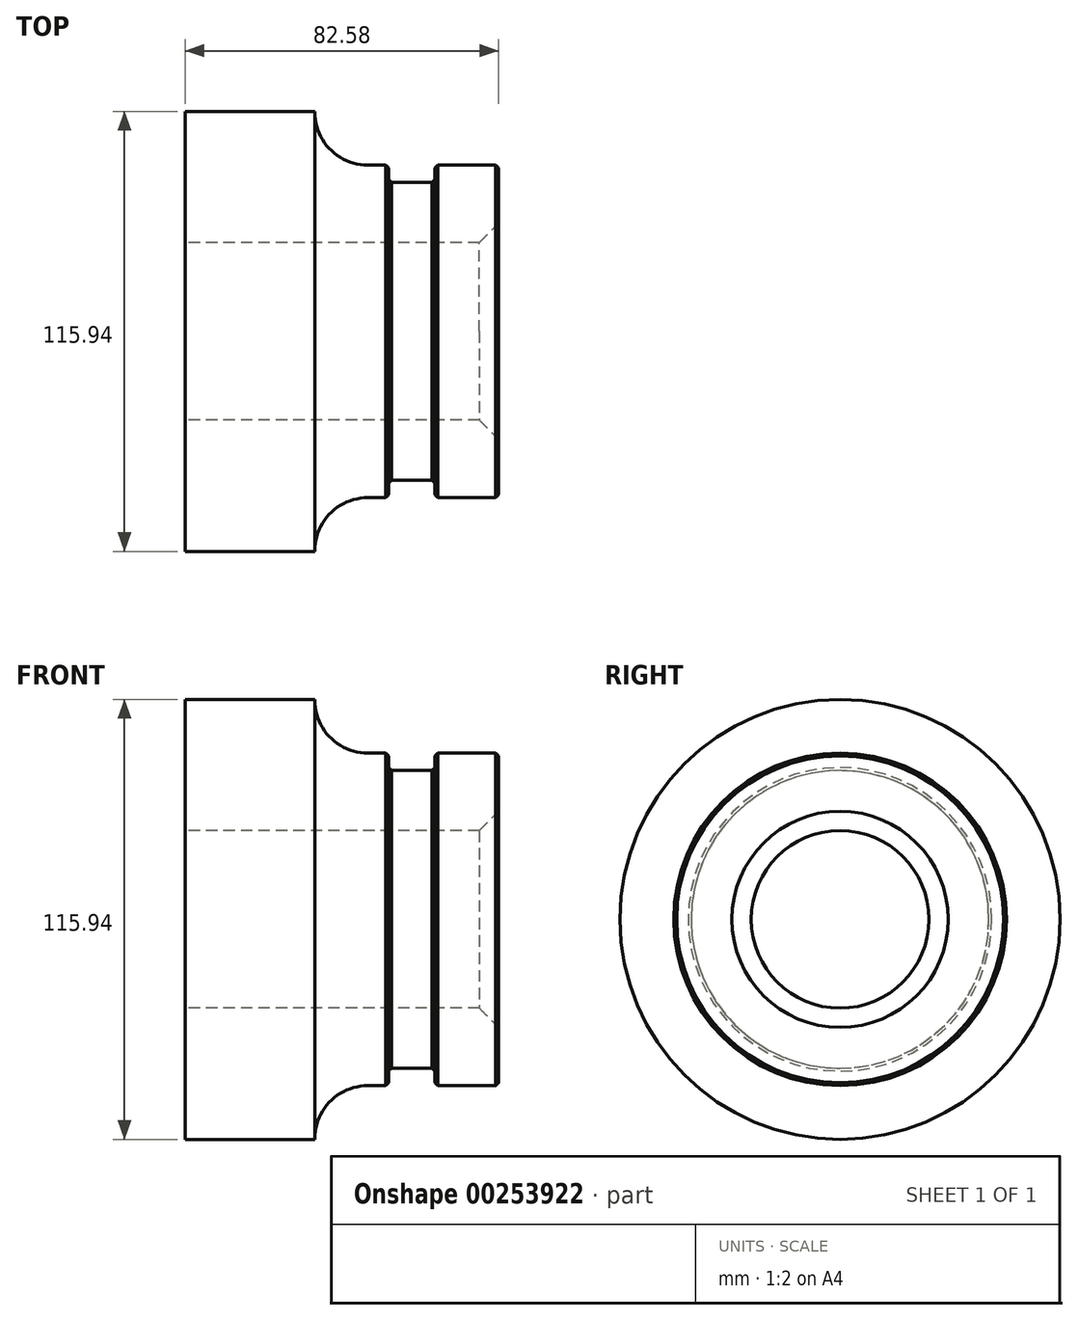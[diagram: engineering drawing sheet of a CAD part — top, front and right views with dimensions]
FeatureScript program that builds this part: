
annotation { "Feature Type Name" : "Feature", "Feature Type Description" : "" }
export const myFeature = defineFeature(function(context is Context, id is Id, definition is map)
    precondition{}
    {
        {
            var Q0;
            Q0=qCreatedBy(makeId("Front.planeOp"),FACE);
            var sketch = newSketch(context, id + "F0", { "sketchPlane" : qUnion([Q0])});
            skLineSegment(sketch, "E0", {"start": v(-43.78, 57.97) * mm, "end": v(-9.65, 57.97) * mm});
            skLineSegment(sketch, "E1", {"start": v(-9.65, 57.97) * mm, "end": v(-9.65, 43.82) * mm});
            skLineSegment(sketch, "E2", {"start": v(-9.65, 43.82) * mm, "end": v(9.8, 43.82) * mm});
            skLineSegment(sketch, "E3", {"start": v(9.8, 43.82) * mm, "end": v(9.8, 39.23) * mm});
            skLineSegment(sketch, "E4", {"start": v(9.8, 39.23) * mm, "end": v(22, 39.23) * mm});
            skLineSegment(sketch, "E5", {"start": v(22, 39.23) * mm, "end": v(22, 43.82) * mm});
            skLineSegment(sketch, "E6", {"start": v(22, 43.82) * mm, "end": v(38.8, 43.82) * mm});
            skLineSegment(sketch, "E7", {"start": v(38.8, 43.82) * mm, "end": v(38.8, 23.4) * mm});
            skLineSegment(sketch, "E8", {"start": v(38.8, 23.4) * mm, "end": v(-43.78, 23.4) * mm});
            skLineSegment(sketch, "E9", {"start": v(-43.78, 23.4) * mm, "end": v(-43.78, 57.97) * mm});
            skLineSegment(sketch, "E10", {"start": v(-43.78, 0) * mm, "end": v(38.8, 0) * mm});
            skSolve(sketch);
        }
        {
            var Q0;
            Q0=makeQuery(id+"F0.imprint","IMPRINT",FACE,{"disambiguationData":[TD([[makeQuery(id+"F0.imprint","IMPRINT",EDGE,{"derivedFrom":sQuery(id+"F0.wireOp",EDGE,"E0")}),-1.0]])]});
            var Q1;
            Q1=sQuery(id+"F0.wireOp",EDGE,"E10");
            revolve(context, id + "F1", {"entities" : qUnion([Q0]), "axis" : qUnion([Q1]), "revolveType" : RevolveType.FULL});
        }
        {
            var Q0;
            Q0=makeQuery(id+"F1.opRevolve","SWEPT_EDGE",EDGE,{"disambiguationData":[OSD([sQuery(id+"F0.wireOp",EDGE,"E6"),sQuery(id+"F0.wireOp",EDGE,"E7")])]});
            var Q1;
            Q1=makeQuery(id+"F1.opRevolve","SWEPT_EDGE",EDGE,{"disambiguationData":[OSD([sQuery(id+"F0.wireOp",EDGE,"E5"),sQuery(id+"F0.wireOp",EDGE,"E6")])]});
            var Q2;
            Q2=makeQuery(id+"F1.opRevolve","SWEPT_EDGE",EDGE,{"disambiguationData":[OSD([sQuery(id+"F0.wireOp",EDGE,"E2"),sQuery(id+"F0.wireOp",EDGE,"E3")])]});
            var Q3;
            Q3=makeQuery(id+"F1.opRevolve","SWEPT_EDGE",EDGE,{"disambiguationData":[OSD([sQuery(id+"F0.wireOp",EDGE,"E3"),sQuery(id+"F0.wireOp",EDGE,"E4")])]});
            var Q4;
            Q4=makeQuery(id+"F1.opRevolve","SWEPT_EDGE",EDGE,{"disambiguationData":[OSD([sQuery(id+"F0.wireOp",EDGE,"E4"),sQuery(id+"F0.wireOp",EDGE,"E5")])]});
            chamfer(context, id + "F2", {"entities" : qUnion([Q0, Q1, Q2, Q3, Q4]), "width" : 0.76 * mm, "tangentPropagation" : true});
        }
        {
            var Q0;
            Q0=makeQuery(id+"F1.opRevolve","SWEPT_EDGE",EDGE,{"disambiguationData":[OSD([sQuery(id+"F0.wireOp",EDGE,"E7"),sQuery(id+"F0.wireOp",EDGE,"E8")])]});
            chamfer(context, id + "F3", {"entities" : qUnion([Q0]), "width" : 5.08 * mm, "tangentPropagation" : true});
        }
        {
            var Q0;
            Q0=makeQuery(id+"F1.opRevolve","SWEPT_EDGE",EDGE,{"disambiguationData":[OSD([sQuery(id+"F0.wireOp",EDGE,"E1"),sQuery(id+"F0.wireOp",EDGE,"E2")])]});
            fillet(context, id + "F4", {"entities" : qUnion([Q0]), "radius" : 13.97 * mm, "tangentPropagation" : true, "allowEdgeOverflow" : false});
        }
    });
